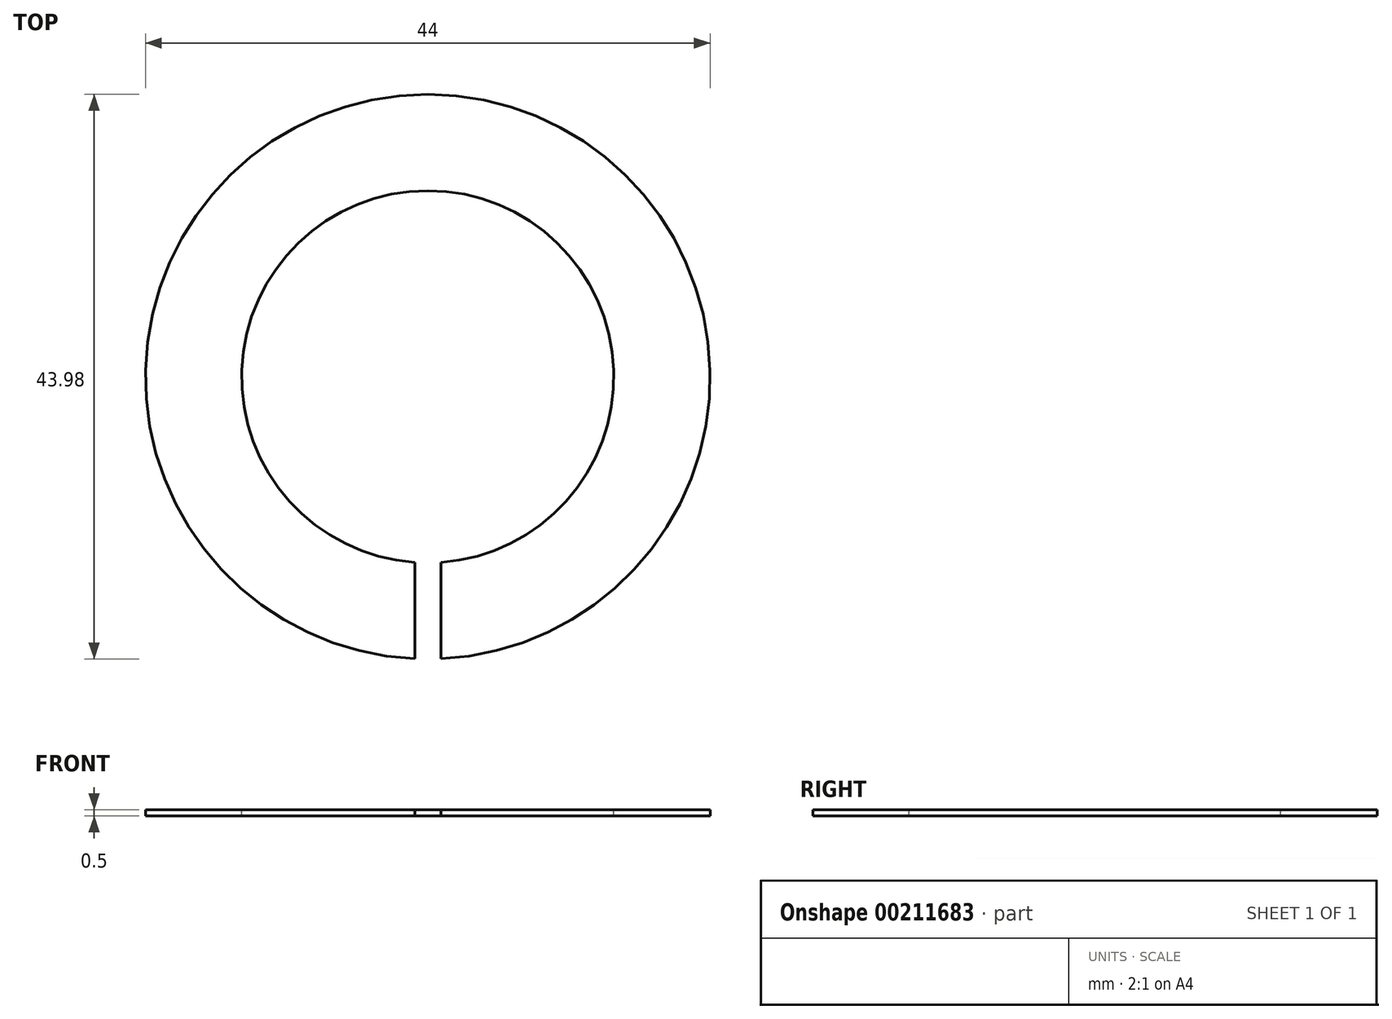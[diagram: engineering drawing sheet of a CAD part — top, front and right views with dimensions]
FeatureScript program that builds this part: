
annotation { "Feature Type Name" : "Feature", "Feature Type Description" : "" }
export const myFeature = defineFeature(function(context is Context, id is Id, definition is map)
    precondition{}
    {
        {
            var Q0;
            Q0=qCreatedBy(makeId("Top.planeOp"),FACE);
            var sketch = newSketch(context, id + "F0", { "sketchPlane" : qUnion([Q0])});
            skCircle(sketch, "E0", {"center": v(0, 0) * mm, "radius": 22 * mm});
            skSolve(sketch);
        }
        {
            var Q0;
            Q0=makeQuery(id+"F0.imprint","IMPRINT",FACE,{"disambiguationData":[TD([[makeQuery(id+"F0.imprint","IMPRINT",EDGE,{"derivedFrom":sQuery(id+"F0.wireOp",EDGE,"E0")}),1.0]])]});
            extrude(context, id + "F1", {"entities" : qUnion([Q0]), "depth" : .5 * mm});
        }
        {
            var Q0;
            Q0=makeQuery(id+"F1.opExtrude","CAP_FACE",FACE,{"disambiguationData":[OSD([sQuery(id+"F0.wireOp",EDGE,"E0")])],"isStart":false});
            var sketch = newSketch(context, id + "F2", { "sketchPlane" : qUnion([Q0])});
            skCircle(sketch, "E1", {"center": v(0, 0) * mm, "radius": 14.5 * mm});
            skSolve(sketch);
        }
        {
            var Q0;
            Q0=makeQuery(id+"F2.imprint","IMPRINT",FACE,{"disambiguationData":[TD([[makeQuery(id+"F2.imprint","IMPRINT",EDGE,{"derivedFrom":sQuery(id+"F2.wireOp",EDGE,"E1")}),1.0]])]});
            extrude(context, id + "F3", {"entities" : qUnion([Q0]), "operationType" : NewBodyOperationType.REMOVE, "oppositeDirection" : true, "depth" : 25 * mm});
        }
        {
            var Q0;
            Q0=makeQuery(id+"F1.opExtrude","CAP_FACE",FACE,{"disambiguationData":[OSD([sQuery(id+"F0.wireOp",EDGE,"E0")])],"isStart":false});
            var sketch = newSketch(context, id + "F4", { "sketchPlane" : qUnion([Q0])});
            skLineSegment(sketch, "E2.bottom", {"start": v(1.02, -24.81) * mm, "end": v(-1.02, -24.81) * mm});
            skLineSegment(sketch, "E2.left", {"start": v(1.02, -24.81) * mm, "end": v(1.02, 24.81) * mm});
            skLineSegment(sketch, "E2.right", {"start": v(-1.02, -24.81) * mm, "end": v(-1.02, 24.81) * mm});
            skPoint(sketch, "E2.middle", {"position": v(0, 0) * mm});
            skLineSegment(sketch, "E3", {"start": v(-1.02, 1.25) * mm, "end": v(1.02, 1.25) * mm});
            skSolve(sketch);
        }
        {
            var Q0;
            {var subQ0=sQuery(id+"F4.wireOp",EDGE,"E2.left");var subQ1=makeQuery(id+"F1.opExtrude","CAP_EDGE",EDGE,{"disambiguationData":[OSD([sQuery(id+"F0.wireOp",EDGE,"E0")])],"isStart":false});var subQ2=makeQuery(id+"F4.imprint","INTERSECT",VERTEX,{"disambiguationData":[OD(1.0)],"derivedFrom":[subQ1,subQ0]});Q0=makeQuery(id+"F4.imprint","IMPRINT",FACE,{"disambiguationData":[TD([[makeQuery(id+"F4.imprint","IMPRINT",EDGE,{"disambiguationData":[TD([[subQ2,-1.0]])],"derivedFrom":subQ0}),1.0]])]});}
            extrude(context, id + "F5", {"entities" : qUnion([Q0]), "operationType" : NewBodyOperationType.REMOVE, "oppositeDirection" : true, "depth" : 25 * mm});
        }
    });
